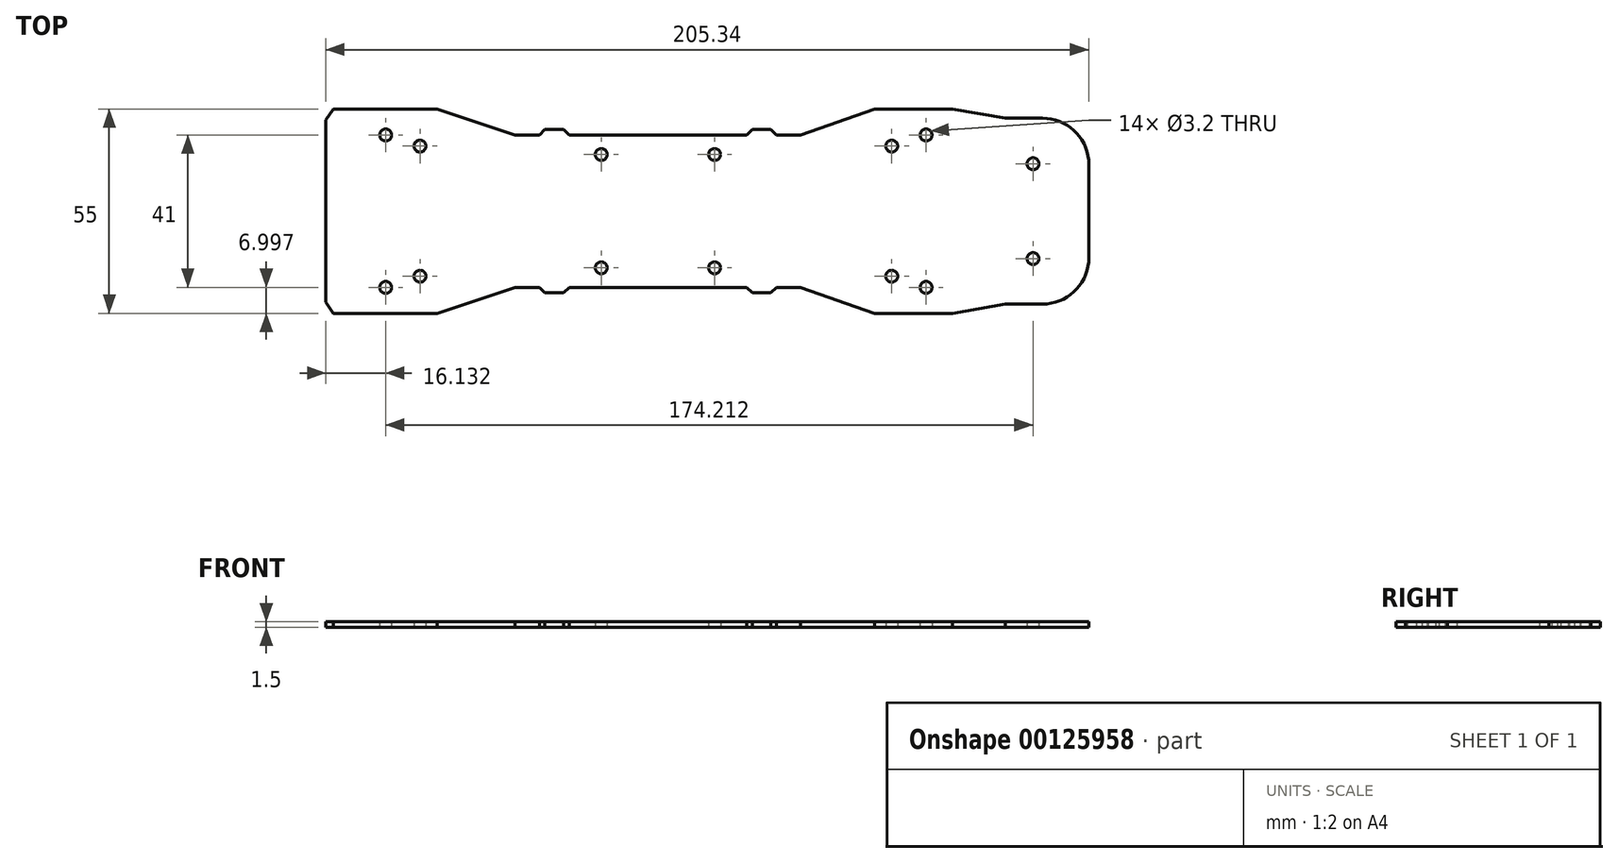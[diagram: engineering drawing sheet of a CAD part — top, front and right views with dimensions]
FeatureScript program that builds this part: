
annotation { "Feature Type Name" : "Feature", "Feature Type Description" : "" }
export const myFeature = defineFeature(function(context is Context, id is Id, definition is map)
    precondition{}
    {
        {
            var Q0;
            Q0=qCreatedBy(makeId("Top.planeOp"),FACE);
            var sketch = newSketch(context, id + "F0", { "sketchPlane" : qUnion([Q0])});
            skLineSegment(sketch, "E0", {"start": v(-6.68, -17.51) * mm, "end": v(-5.18, -16.01) * mm});
            skLineSegment(sketch, "E1", {"start": v(-62.48, 26.49) * mm, "end": v(-60.98, 24.99) * mm});
            skLineSegment(sketch, "E2", {"start": v(-96.48, 31.99) * mm, "end": v(-75.48, 24.99) * mm});
            skLineSegment(sketch, "E3", {"start": v(42.22, -23.01) * mm, "end": v(56.42, -20.51) * mm});
            skLineSegment(sketch, "E4", {"start": v(-9.18, -17.51) * mm, "end": v(-6.68, -17.51) * mm});
            skArc(sketch, "E5", {"start": v(66.42, -20.51) * mm, "mid": v(74.83, -17.27) * mm, "end": v(78.86, -9.21) * mm});
            skLineSegment(sketch, "E6", {"start": v(-126.48, 28.99) * mm, "end": v(-126.48, -20.01) * mm});
            skLineSegment(sketch, "E7", {"start": v(56.42, 29.49) * mm, "end": v(66.42, 29.49) * mm});
            skLineSegment(sketch, "E8", {"start": v(-75.48, -16.01) * mm, "end": v(-68.98, -16.01) * mm});
            skLineSegment(sketch, "E9", {"start": v(1.32, 24.99) * mm, "end": v(21.22, 31.99) * mm});
            skLineSegment(sketch, "E10", {"start": v(-124.48, 31.99) * mm, "end": v(-126.48, 28.99) * mm});
            skCircle(sketch, "E11", {"center": v(63.86, 17.24) * mm, "radius": 1.6 * mm});
            skCircle(sketch, "E12", {"center": v(-52.33, 19.74) * mm, "radius": 1.6 * mm});
            skLineSegment(sketch, "E13", {"start": v(-6.68, 26.49) * mm, "end": v(-5.18, 24.99) * mm});
            skCircle(sketch, "E14", {"center": v(-21.83, 19.74) * mm, "radius": 1.6 * mm});
            skLineSegment(sketch, "E15", {"start": v(-67.48, 26.49) * mm, "end": v(-68.98, 24.99) * mm});
            skLineSegment(sketch, "E16", {"start": v(-9.18, 26.49) * mm, "end": v(-11.68, 26.49) * mm});
            skLineSegment(sketch, "E17", {"start": v(-11.68, 26.49) * mm, "end": v(-13.18, 24.99) * mm});
            skLineSegment(sketch, "E18", {"start": v(-64.98, 26.49) * mm, "end": v(-62.48, 26.49) * mm});
            skLineSegment(sketch, "E19", {"start": v(-5.18, 24.99) * mm, "end": v(1.32, 24.99) * mm});
            skLineSegment(sketch, "E20", {"start": v(-11.68, -17.51) * mm, "end": v(-13.18, -16.01) * mm});
            skLineSegment(sketch, "E21", {"start": v(-9.18, -17.51) * mm, "end": v(-11.68, -17.51) * mm});
            skLineSegment(sketch, "E22", {"start": v(42.22, 31.99) * mm, "end": v(56.42, 29.49) * mm});
            skLineSegment(sketch, "E23", {"start": v(-64.98, -17.51) * mm, "end": v(-62.48, -17.51) * mm});
            skLineSegment(sketch, "E24", {"start": v(-67.48, -17.51) * mm, "end": v(-68.98, -16.01) * mm});
            skLineSegment(sketch, "E25", {"start": v(1.32, -16.01) * mm, "end": v(21.22, -23.01) * mm});
            skLineSegment(sketch, "E26", {"start": v(56.42, -20.51) * mm, "end": v(66.42, -20.51) * mm});
            skCircle(sketch, "E27", {"center": v(-21.83, -10.76) * mm, "radius": 1.6 * mm});
            skCircle(sketch, "E28", {"center": v(-52.33, -10.76) * mm, "radius": 1.6 * mm});
            skLineSegment(sketch, "E29", {"start": v(-5.18, -16.01) * mm, "end": v(1.32, -16.01) * mm});
            skCircle(sketch, "E30", {"center": v(63.86, -8.26) * mm, "radius": 1.6 * mm});
            skLineSegment(sketch, "E31", {"start": v(-60.98, -16.01) * mm, "end": v(-13.18, -16.01) * mm});
            skLineSegment(sketch, "E32", {"start": v(-96.48, -23.01) * mm, "end": v(-75.48, -16.01) * mm});
            skLineSegment(sketch, "E33", {"start": v(78.86, 18.19) * mm, "end": v(78.86, -9.21) * mm});
            skArc(sketch, "E34", {"start": v(78.86, 18.19) * mm, "mid": v(74.83, 26.24) * mm, "end": v(66.42, 29.49) * mm});
            skLineSegment(sketch, "E35", {"start": v(-64.98, 26.49) * mm, "end": v(-67.48, 26.49) * mm});
            skLineSegment(sketch, "E36", {"start": v(-9.18, 26.49) * mm, "end": v(-6.68, 26.49) * mm});
            skLineSegment(sketch, "E37", {"start": v(-64.98, -17.51) * mm, "end": v(-67.48, -17.51) * mm});
            skLineSegment(sketch, "E38", {"start": v(-124.48, -23.01) * mm, "end": v(-126.48, -20.01) * mm});
            skLineSegment(sketch, "E39", {"start": v(-75.48, 24.99) * mm, "end": v(-68.98, 24.99) * mm});
            skLineSegment(sketch, "E40", {"start": v(-60.98, 24.99) * mm, "end": v(-13.18, 24.99) * mm});
            skLineSegment(sketch, "E41", {"start": v(-62.48, -17.51) * mm, "end": v(-60.98, -16.01) * mm});
            skLineSegment(sketch, "E42", {"start": v(-124.48, -23.01) * mm, "end": v(-116.48, -23.01) * mm});
            skLineSegment(sketch, "E43", {"start": v(-55.68, 4.49) * mm, "end": v(-42.9, 4.49) * mm, "construction": true});
            skLineSegment(sketch, "E44.MirrorCS", {"start": v(-124.48, 31.99) * mm, "end": v(-116.48, 31.99) * mm});
            skLineSegment(sketch, "E45", {"start": v(-37.63, -34.38) * mm, "end": v(-37.63, -40.55) * mm, "construction": true});
            skLineSegment(sketch, "E46", {"start": v(-116.48, 31.99) * mm, "end": v(-96.48, 31.99) * mm});
            skLineSegment(sketch, "E47", {"start": v(-96.48, -23.01) * mm, "end": v(-116.48, -23.01) * mm});
            skLineSegment(sketch, "E48", {"start": v(21.22, -23.01) * mm, "end": v(42.22, -23.01) * mm});
            skLineSegment(sketch, "E49", {"start": v(42.22, 31.99) * mm, "end": v(21.22, 31.99) * mm});
            skCircle(sketch, "E50", {"center": v(-110.35, -16.01) * mm, "radius": 1.6 * mm});
            skCircle(sketch, "E51", {"center": v(-101.13, -13.01) * mm, "radius": 1.6 * mm});
            skPoint(sketch, "E52.visualSharp", {"position": v(-115.3, -9.57) * mm});
            skPoint(sketch, "E53.visualSharp", {"position": v(-94.75, -3.24) * mm});
            skLineSegment(sketch, "E54", {"start": v(-116.48, -23.01) * mm, "end": v(-115.48, -11.58) * mm, "construction": true});
            skLineSegment(sketch, "E55", {"start": v(-113.38, -8.98) * mm, "end": v(-99.01, -4.55) * mm, "construction": true});
            skLineSegment(sketch, "E56", {"start": v(-95.14, -7.68) * mm, "end": v(-96.48, -23.01) * mm, "construction": true});
            skCircle(sketch, "E57.MirrorC", {"center": v(-110.35, 24.99) * mm, "radius": 1.6 * mm});
            skCircle(sketch, "E58.MirrorC", {"center": v(-101.13, 21.99) * mm, "radius": 1.6 * mm});
            skCircle(sketch, "E59.MirrorC", {"center": v(25.86, -13.01) * mm, "radius": 1.6 * mm});
            skCircle(sketch, "E60.MirrorC", {"center": v(25.86, 21.99) * mm, "radius": 1.6 * mm});
            skCircle(sketch, "E61.MirrorC", {"center": v(35.09, 24.99) * mm, "radius": 1.6 * mm});
            skCircle(sketch, "E62.MirrorC", {"center": v(35.09, -16.01) * mm, "radius": 1.6 * mm});
            skArc(sketch, "E63.filletArc", {"start": v(-113.38, -8.98) * mm, "mid": v(-114.83, -9.96) * mm, "end": v(-115.48, -11.58) * mm, "construction": true});
            skArc(sketch, "E64.filletArc", {"start": v(-95.14, -7.68) * mm, "mid": v(-96.24, -5.08) * mm, "end": v(-99.01, -4.55) * mm, "construction": true});
            skSolve(sketch);
        }
        {
            var Q0;
            Q0=makeQuery(id+"F0.imprint","IMPRINT",FACE,{"disambiguationData":[TD([[makeQuery(id+"F0.imprint","IMPRINT",EDGE,{"derivedFrom":sQuery(id+"F0.wireOp",EDGE,"E0")}),1.0]])]});
            extrude(context, id + "F1", {"entities" : qUnion([Q0]), "depth" : 1.5 * mm});
        }
    });
